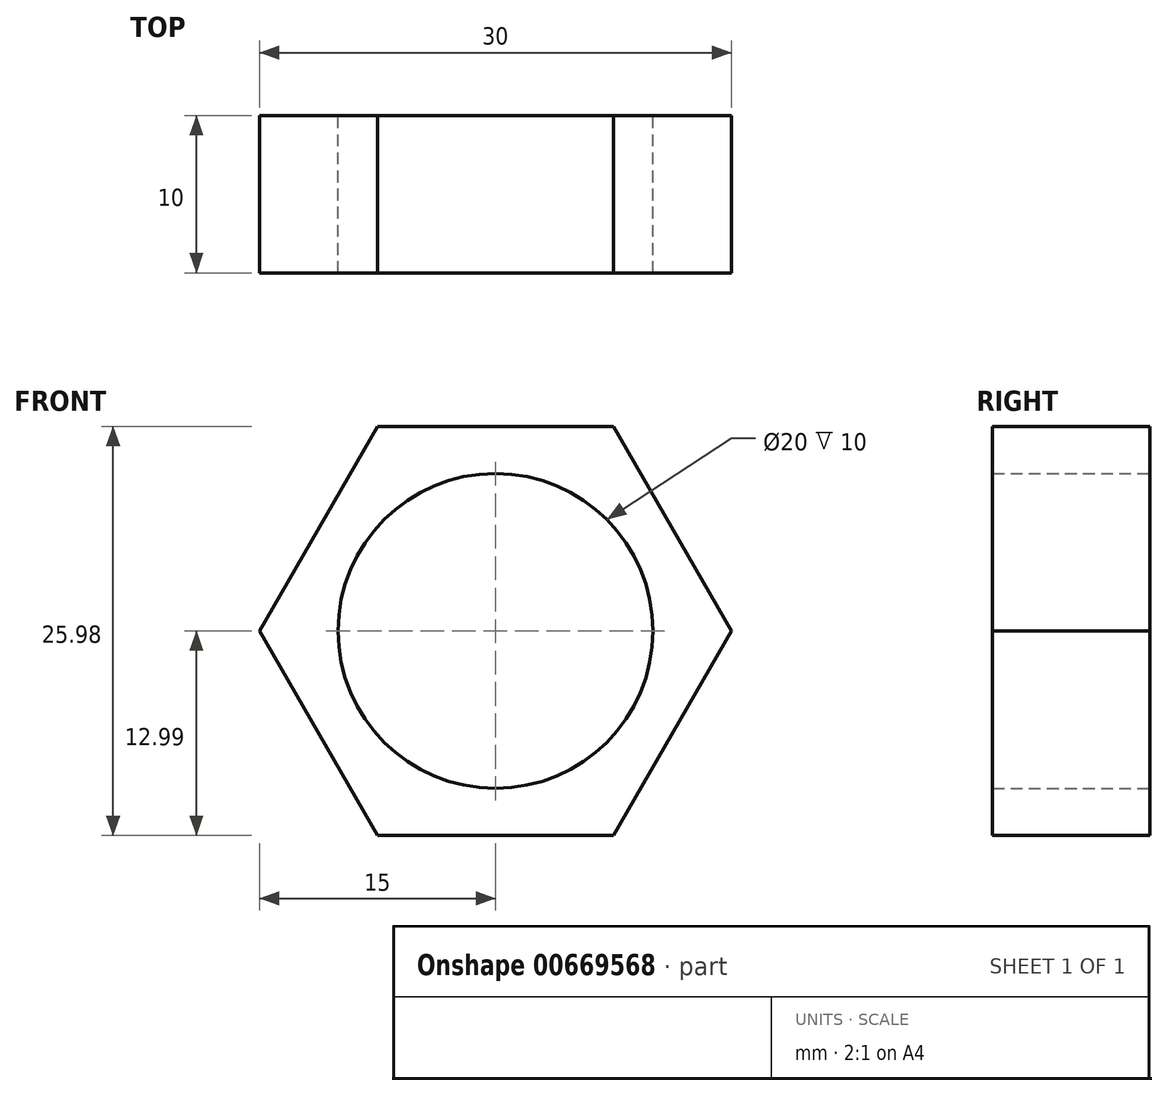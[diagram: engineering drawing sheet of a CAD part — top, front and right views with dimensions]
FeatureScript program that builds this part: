
annotation { "Feature Type Name" : "Feature", "Feature Type Description" : "" }
export const myFeature = defineFeature(function(context is Context, id is Id, definition is map)
    precondition{}
    {
        {
            var Q0;
            Q0=qCreatedBy(makeId("Front.planeOp"),FACE);
            var sketch = newSketch(context, id + "F0", { "sketchPlane" : qUnion([Q0])});
            skCircle(sketch, "E0.cCircle", {"center": v(-147.43, 0) * mm, "radius": 13 * mm, "construction": true});
            skLineSegment(sketch, "E0.0", {"start": v(-139.93, -13) * mm, "end": v(-154.93, -13) * mm});
            skLineSegment(sketch, "E0.1", {"start": v(-154.93, -13) * mm, "end": v(-162.43, 0) * mm});
            skLineSegment(sketch, "E0.2", {"start": v(-162.43, 0) * mm, "end": v(-154.93, 13) * mm});
            skLineSegment(sketch, "E0.3", {"start": v(-154.93, 13) * mm, "end": v(-139.93, 13) * mm});
            skLineSegment(sketch, "E0.4", {"start": v(-139.93, 13) * mm, "end": v(-132.43, 0) * mm});
            skLineSegment(sketch, "E0.5", {"start": v(-132.43, 0) * mm, "end": v(-139.93, -13) * mm});
            skPoint(sketch, "E0.0.midPoint", {"position": v(-147.43, -13) * mm});
            skCircle(sketch, "E1", {"center": v(-147.43, 0) * mm, "radius": 10 * mm});
            skCircle(sketch, "E2.cCircle", {"center": v(-86.74, 3.46) * mm, "radius": 13 * mm, "construction": true});
            skLineSegment(sketch, "E2.0", {"start": v(-79.24, -9.53) * mm, "end": v(-94.24, -9.53) * mm});
            skLineSegment(sketch, "E2.1", {"start": v(-94.24, -9.53) * mm, "end": v(-101.74, 3.46) * mm});
            skLineSegment(sketch, "E2.2", {"start": v(-101.74, 3.46) * mm, "end": v(-94.24, 16.45) * mm});
            skLineSegment(sketch, "E2.3", {"start": v(-94.24, 16.45) * mm, "end": v(-79.24, 16.45) * mm});
            skLineSegment(sketch, "E2.4", {"start": v(-79.24, 16.45) * mm, "end": v(-71.74, 3.46) * mm});
            skLineSegment(sketch, "E2.5", {"start": v(-71.74, 3.46) * mm, "end": v(-79.24, -9.53) * mm});
            skPoint(sketch, "E2.0.midPoint", {"position": v(-86.74, -9.53) * mm});
            skCircle(sketch, "E3", {"center": v(-86.74, 3.46) * mm, "radius": 10 * mm});
            skSolve(sketch);
        }
        {
            var Q0;
            Q0=makeQuery(id+"F0.imprint","IMPRINT",FACE,{"disambiguationData":[TD([[makeQuery(id+"F0.imprint","IMPRINT",EDGE,{"derivedFrom":sQuery(id+"F0.wireOp",EDGE,"E0.0")}),-1.0]])]});
            extrude(context, id + "F1", {"entities" : qUnion([Q0]), "depth" : 10 * mm, "offsetDistance" : 25 * mm});
        }
    });
